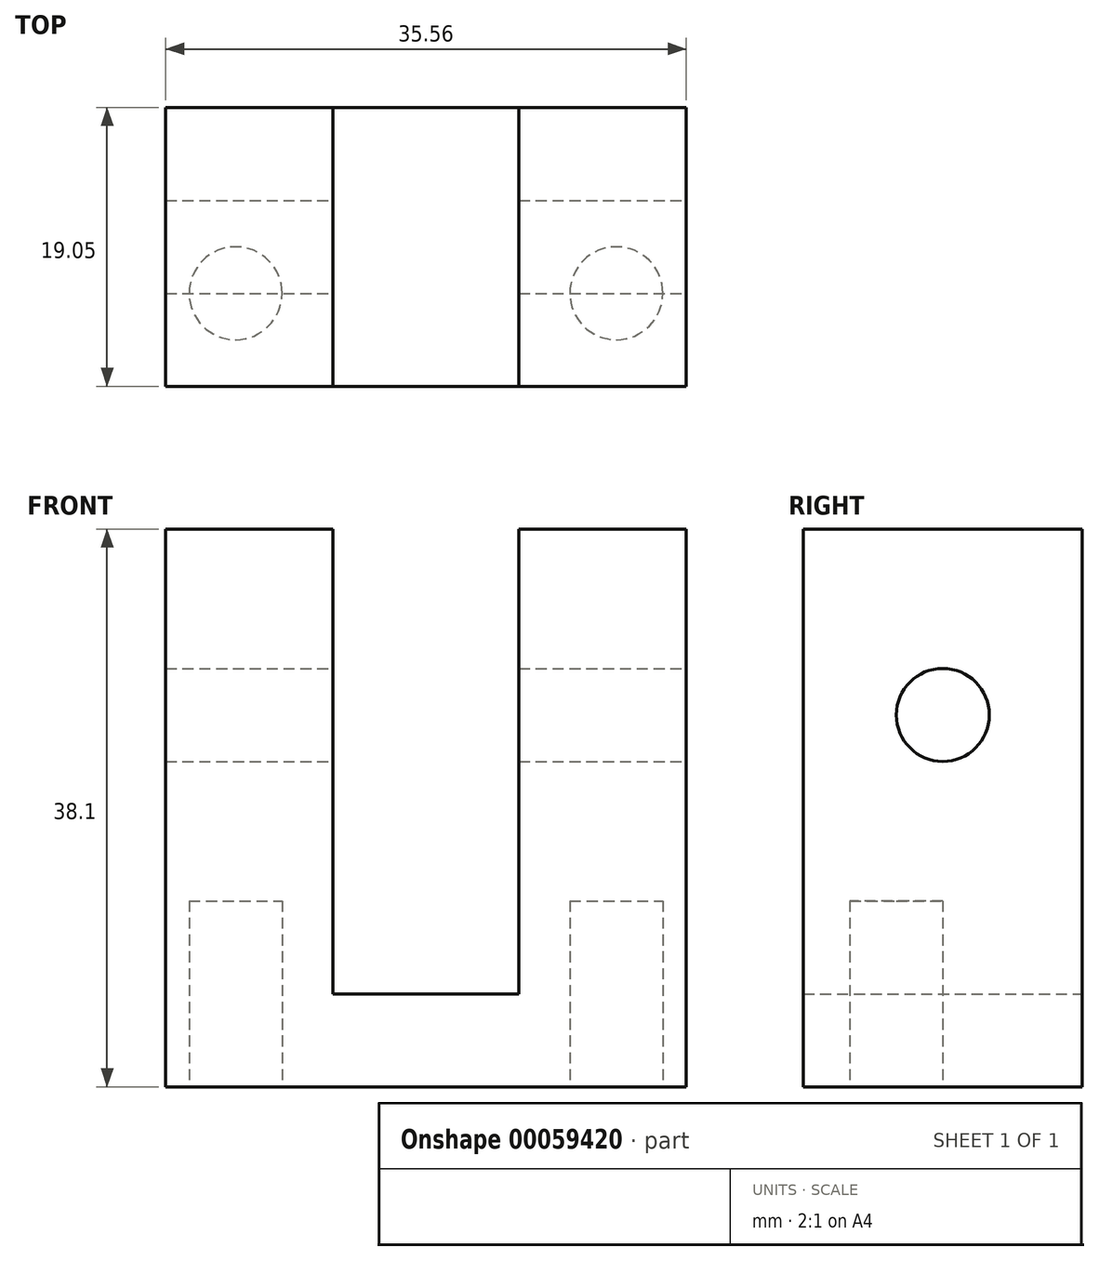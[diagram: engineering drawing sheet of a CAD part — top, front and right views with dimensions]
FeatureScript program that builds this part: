
annotation { "Feature Type Name" : "Feature", "Feature Type Description" : "" }
export const myFeature = defineFeature(function(context is Context, id is Id, definition is map)
    precondition{}
    {
        {
            var Q0;
            Q0=qCreatedBy(makeId("Front.planeOp"),FACE);
            var sketch = newSketch(context, id + "F0", { "sketchPlane" : qUnion([Q0])});
            skLineSegment(sketch, "E0.bottom", {"start": v(0, 0) * mm, "end": v(35.56, 0) * mm});
            skLineSegment(sketch, "E0.top", {"start": v(0, 38.1) * mm, "end": v(11.43, 38.1) * mm});
            skLineSegment(sketch, "E0.left", {"start": v(0, 0) * mm, "end": v(0, 38.1) * mm});
            skLineSegment(sketch, "E0.right", {"start": v(35.56, 0) * mm, "end": v(35.56, 38.1) * mm});
            skLineSegment(sketch, "E1", {"start": v(11.43, 38.1) * mm, "end": v(11.43, 6.35) * mm});
            skLineSegment(sketch, "E2", {"start": v(11.43, 6.35) * mm, "end": v(24.13, 6.35) * mm});
            skLineSegment(sketch, "E3", {"start": v(24.13, 6.35) * mm, "end": v(24.13, 38.1) * mm});
            skLineSegment(sketch, "E4.trimOffspring", {"start": v(24.13, 38.1) * mm, "end": v(35.56, 38.1) * mm});
            skSolve(sketch);
        }
        {
            var Q0;
            Q0 = qSketchRegion(id + "F0", true);
            var Q1;
            Q1=makeQuery(id+"F0.imprint","IMPRINT",FACE,{"disambiguationData":[TD([[makeQuery(id+"F0.imprint","IMPRINT",EDGE,{"derivedFrom":sQuery(id+"F0.wireOp",EDGE,"E0.bottom")}),1.0]])]});
            extrude(context, id + "F1", {"entities" : qUnion([Q0, Q1]), "depth" : 19.05 * mm});
        }
        {
            var Q0;
            Q0=makeQuery(id+"F1.opExtrude","SWEPT_FACE",FACE,{"disambiguationData":[OSD([sQuery(id+"F0.wireOp",EDGE,"E0.right")])]});
            var sketch = newSketch(context, id + "F2", { "sketchPlane" : qUnion([Q0])});
            skCircle(sketch, "E5", {"center": v(-9.53, 25.4) * mm, "radius": 3.18 * mm});
            skSolve(sketch);
        }
        {
            var Q0;
            Q0 = qSketchRegion(id + "F2", true);
            extrude(context, id + "F3", {"entities" : qUnion([Q0]), "operationType" : NewBodyOperationType.REMOVE, "endBound" : BoundingType.THROUGH_ALL, "oppositeDirection" : true, "depth" : 25.4 * mm});
        }
        {
            var Q0;
            Q0=makeQuery(id+"F1.opExtrude","SWEPT_FACE",FACE,{"disambiguationData":[OSD([sQuery(id+"F0.wireOp",EDGE,"E0.bottom")])]});
            var sketch = newSketch(context, id + "F4", { "sketchPlane" : qUnion([Q0])});
            skCircle(sketch, "E6", {"center": v(4.78, 12.7) * mm, "radius": 3.18 * mm});
            skCircle(sketch, "E7", {"center": v(30.78, 12.7) * mm, "radius": 3.18 * mm});
            skSolve(sketch);
        }
        {
            var Q0;
            Q0 = qSketchRegion(id + "F4", true);
            extrude(context, id + "F5", {"entities" : qUnion([Q0]), "operationType" : NewBodyOperationType.REMOVE, "oppositeDirection" : true, "depth" : 12.7 * mm});
        }
    });
